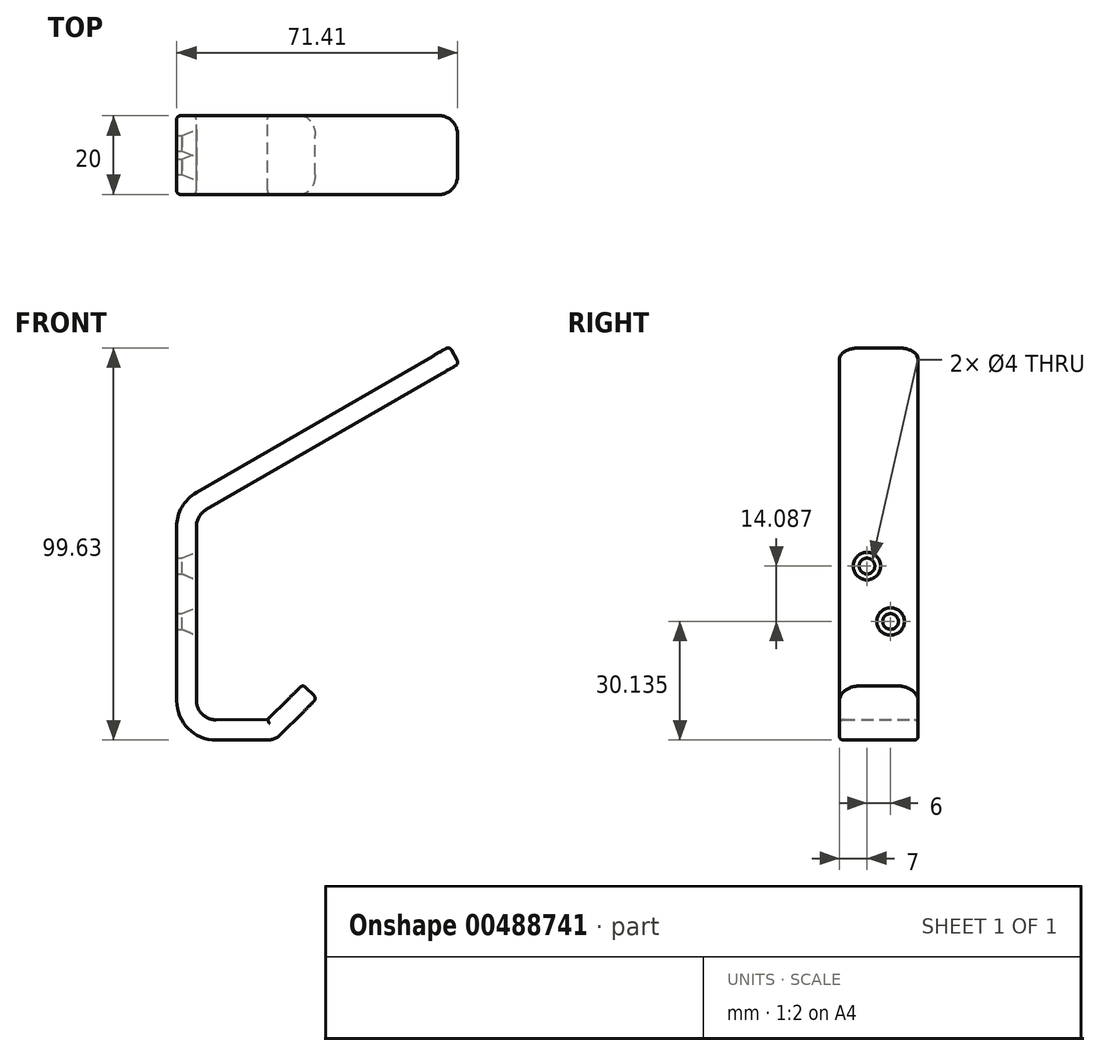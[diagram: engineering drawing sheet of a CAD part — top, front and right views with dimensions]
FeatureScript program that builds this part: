
annotation { "Feature Type Name" : "Feature", "Feature Type Description" : "" }
export const myFeature = defineFeature(function(context is Context, id is Id, definition is map)
    precondition{}
    {
        {
            var Q0;
            Q0=qCreatedBy(makeId("Front.planeOp"),FACE);
            var sketch = newSketch(context, id + "F0", { "sketchPlane" : qUnion([Q0])});
            skLineSegment(sketch, "E0", {"start": v(-14.58, -41.38) * mm, "end": v(-14.58, 18.62) * mm});
            skLineSegment(sketch, "E1", {"start": v(-14.58, -41.38) * mm, "end": v(10.42, -41.38) * mm});
            skLineSegment(sketch, "E2", {"start": v(10.42, -41.38) * mm, "end": v(21.02, -30.78) * mm});
            skLineSegment(sketch, "E3", {"start": v(-14.58, 18.62) * mm, "end": v(54.7, 58.62) * mm});
            skLineSegment(sketch, "E4", {"start": v(54.7, 58.62) * mm, "end": v(57.2, 54.29) * mm});
            skLineSegment(sketch, "E5", {"start": v(57.2, 54.29) * mm, "end": v(-9.58, 15.73) * mm});
            skLineSegment(sketch, "E6", {"start": v(21.02, -30.78) * mm, "end": v(17.49, -27.24) * mm});
            skLineSegment(sketch, "E7", {"start": v(17.49, -27.24) * mm, "end": v(8.54, -36.19) * mm});
            skLineSegment(sketch, "E8", {"start": v(-9.58, -36.27) * mm, "end": v(-9.58, 15.73) * mm});
            skPoint(sketch, "E9.endSnap0", {"position": v(15.72, -36.08) * mm});
            skPoint(sketch, "E10.orphan", {"position": v(43.36, -36.08) * mm});
            skLineSegment(sketch, "E11.trimOffspring", {"start": v(-9.58, -36.27) * mm, "end": v(8.54, -36.19) * mm});
            skPoint(sketch, "E12.trimOffspring.end.orphan", {"position": v(31.93, -36.08) * mm});
            skSolve(sketch);
        }
        {
            var Q0;
            Q0 = qSketchRegion(id + "F0", true);
            extrude(context, id + "F1", {"entities" : qUnion([Q0]), "depth" : 20 * mm});
        }
        {
            var Q0;
            Q0=makeQuery(id+"F1.opExtrude","SWEPT_EDGE",EDGE,{"disambiguationData":[OSD([sQuery(id+"F0.wireOp",EDGE,"E0"),sQuery(id+"F0.wireOp",EDGE,"E1")])]});
            fillet(context, id + "F2", {"entities" : qUnion([Q0]), "radius" : 10 * mm, "tangentPropagation" : true, "allowEdgeOverflow" : false});
        }
        {
            var Q0;
            Q0=makeQuery(id+"F1.opExtrude","SWEPT_EDGE",EDGE,{"disambiguationData":[OSD([sQuery(id+"F0.wireOp",EDGE,"E8"),sQuery(id+"F0.wireOp",EDGE,"E11.trimOffspring")])]});
            fillet(context, id + "F3", {"entities" : qUnion([Q0]), "radius" : 5 * mm, "tangentPropagation" : true, "allowEdgeOverflow" : false});
        }
        {
            var Q0;
            Q0=makeQuery(id+"F1.opExtrude","SWEPT_EDGE",EDGE,{"disambiguationData":[OSD([sQuery(id+"F0.wireOp",EDGE,"E5"),sQuery(id+"F0.wireOp",EDGE,"E8")])]});
            fillet(context, id + "F4", {"entities" : qUnion([Q0]), "radius" : 5 * mm, "tangentPropagation" : true, "allowEdgeOverflow" : false});
        }
        {
            var Q0;
            Q0=makeQuery(id+"F1.opExtrude","SWEPT_EDGE",EDGE,{"disambiguationData":[OSD([sQuery(id+"F0.wireOp",EDGE,"E0"),sQuery(id+"F0.wireOp",EDGE,"E3")])]});
            fillet(context, id + "F5", {"entities" : qUnion([Q0]), "radius" : 10 * mm, "tangentPropagation" : true, "allowEdgeOverflow" : false});
        }
        {
            var Q0;
            Q0=makeQuery(id+"F1.opExtrude","CAP_EDGE",EDGE,{"disambiguationData":[OSD([sQuery(id+"F0.wireOp",EDGE,"E6")])],"isStart":true});
            fillet(context, id + "F6", {"entities" : qUnion([Q0]), "radius" : 5 * mm, "tangentPropagation" : true, "allowEdgeOverflow" : false});
        }
        {
            var Q0;
            Q0=makeQuery(id+"F1.opExtrude","CAP_EDGE",EDGE,{"disambiguationData":[OSD([sQuery(id+"F0.wireOp",EDGE,"E6")])],"isStart":false});
            fillet(context, id + "F7", {"entities" : qUnion([Q0]), "radius" : 5 * mm, "tangentPropagation" : true, "allowEdgeOverflow" : false});
        }
        {
            var Q0;
            Q0=makeQuery(id+"F1.opExtrude","CAP_EDGE",EDGE,{"disambiguationData":[OSD([sQuery(id+"F0.wireOp",EDGE,"E4")])],"isStart":true});
            fillet(context, id + "F8", {"entities" : qUnion([Q0]), "radius" : 5 * mm, "tangentPropagation" : true, "allowEdgeOverflow" : false});
        }
        {
            var Q0;
            Q0=makeQuery(id+"F1.opExtrude","CAP_EDGE",EDGE,{"disambiguationData":[OSD([sQuery(id+"F0.wireOp",EDGE,"E4")])],"isStart":false});
            fillet(context, id + "F9", {"entities" : qUnion([Q0]), "radius" : 5 * mm, "tangentPropagation" : true, "allowEdgeOverflow" : false});
        }
        {
            var Q0;
            Q0=makeQuery(id+"F1.opExtrude","SWEPT_EDGE",EDGE,{"disambiguationData":[OSD([sQuery(id+"F0.wireOp",EDGE,"E1"),sQuery(id+"F0.wireOp",EDGE,"E2")])]});
            fillet(context, id + "F10", {"entities" : qUnion([Q0]), "radius" : 5 * mm, "tangentPropagation" : true, "allowEdgeOverflow" : false});
        }
        {
            var Q0;
            Q0=makeQuery(id+"F1.opExtrude","CAP_EDGE",EDGE,{"disambiguationData":[OSD([sQuery(id+"F0.wireOp",EDGE,"E5")])],"isStart":false});
            fillet(context, id + "F11", {"entities" : qUnion([Q0]), "radius" : 1 * mm, "tangentPropagation" : true, "allowEdgeOverflow" : false});
        }
        {
            var Q0;
            Q0=makeQuery(id+"F1.opExtrude","CAP_EDGE",EDGE,{"disambiguationData":[OSD([sQuery(id+"F0.wireOp",EDGE,"E3")])],"isStart":false});
            fillet(context, id + "F12", {"entities" : qUnion([Q0]), "radius" : 1 * mm, "tangentPropagation" : true, "allowEdgeOverflow" : false});
        }
        {
            var Q0;
            Q0=makeQuery(id+"F1.opExtrude","CAP_EDGE",EDGE,{"disambiguationData":[OSD([sQuery(id+"F0.wireOp",EDGE,"E7")])],"isStart":false});
            fillet(context, id + "F13", {"entities" : qUnion([Q0]), "radius" : 1 * mm, "tangentPropagation" : true, "allowEdgeOverflow" : false});
        }
        {
            var Q0;
            Q0=makeQuery(id+"F1.opExtrude","SWEPT_FACE",FACE,{"disambiguationData":[OSD([sQuery(id+"F0.wireOp",EDGE,"E8")])]});
            var sketch = newSketch(context, id + "F14", { "sketchPlane" : qUnion([Q0])});
            skPoint(sketch, "E13", {"position": v(-13, 2.84) * mm});
            skPoint(sketch, "E14", {"position": v(-7, -11.24) * mm});
            skSolve(sketch);
        }
        {
            var Q0;
            Q0=sQuery(id+"F14.wireOp",VERTEX,"E14");
            var Q1;
            Q1=makeQuery(id+"F1.opExtrude","SWEPT_BODY",BODY,{"disambiguationData":[OSD([sQuery(id+"F0.wireOp",EDGE,"E0"),sQuery(id+"F0.wireOp",EDGE,"E1"),sQuery(id+"F0.wireOp",EDGE,"E2"),sQuery(id+"F0.wireOp",EDGE,"E3"),sQuery(id+"F0.wireOp",EDGE,"E4"),sQuery(id+"F0.wireOp",EDGE,"E5"),sQuery(id+"F0.wireOp",EDGE,"E6"),sQuery(id+"F0.wireOp",EDGE,"E7"),sQuery(id+"F0.wireOp",EDGE,"E8"),sQuery(id+"F0.wireOp",EDGE,"E11.trimOffspring")])]});
            hole(context, id + "F15", {"style" : HoleStyle.C_SINK, "endStyle" : HoleEndStyle.THROUGH, "holeDiameter" : 4 * mm, "cSinkDiameter" : 7 * mm, "cSinkAngle" : 45 * degree, "isTappedThrough" : true, "tappedDepth" : 12 * mm, "tapClearance" : 3, "locations" : qUnion([Q0]), "scope" : qUnion([Q1])});
        }
        {
            var Q0;
            Q0=sQuery(id+"F14.wireOp",VERTEX,"E13");
            var Q1;
            Q1=makeQuery(id+"F1.opExtrude","SWEPT_BODY",BODY,{"disambiguationData":[OSD([sQuery(id+"F0.wireOp",EDGE,"E0"),sQuery(id+"F0.wireOp",EDGE,"E1"),sQuery(id+"F0.wireOp",EDGE,"E2"),sQuery(id+"F0.wireOp",EDGE,"E3"),sQuery(id+"F0.wireOp",EDGE,"E4"),sQuery(id+"F0.wireOp",EDGE,"E5"),sQuery(id+"F0.wireOp",EDGE,"E6"),sQuery(id+"F0.wireOp",EDGE,"E7"),sQuery(id+"F0.wireOp",EDGE,"E8"),sQuery(id+"F0.wireOp",EDGE,"E11.trimOffspring")])]});
            hole(context, id + "F16", {"style" : HoleStyle.C_SINK, "endStyle" : HoleEndStyle.THROUGH, "holeDiameter" : 4 * mm, "cSinkDiameter" : 7 * mm, "cSinkAngle" : 45 * degree, "isTappedThrough" : true, "tappedDepth" : 12 * mm, "tapClearance" : 3, "locations" : qUnion([Q0]), "scope" : qUnion([Q1])});
        }
    });
